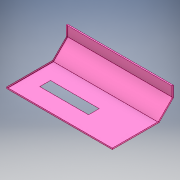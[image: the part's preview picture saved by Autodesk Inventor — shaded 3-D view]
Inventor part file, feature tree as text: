
AUTODESK INVENTOR PART (.ipt)
format: ipt  version: 2018 (Build 220112000, 112)  size: 258,560 bytes
history: native  units: mm
features: sheet_metal_op x13, sketch x6, other x5, extrude x1
ambient origin geometry x8: Origin, YZ Plane, XZ Plane, XY Plane, X Axis, Y Axis, Z Axis, Center Point
bodies: Solid1 (feature_tree)
feature tree (25):
  sheet_metal_op  "Face1"
  sheet_metal_op  "Flange1"
  sheet_metal_op  "Flange2"
  sheet_metal_op  "Flange3"
  extrude  "Extrusion1"  Depth=625.0mm
  sheet_metal_op  "Flange4"
  sketch  "Sketch1"  dims[d0=1410.0mm d1=625.0mm]
  other  "Plate1"
  sketch  "Sketch2"  dims[d2=1.6mm]
  other  "Plate2"
  sheet_metal_op  "Bend1"
  sheet_metal_op  "Corner1"
  sketch  "Sketch3"  dims[d3=1.6mm]
  other  "Plate3"
  sheet_metal_op  "Bend2"
  sheet_metal_op  "Corner2"
  sketch  "Sketch4"  dims[d4=0.8mm]
  other  "Plate4"
  sheet_metal_op  "Bend3"
  sheet_metal_op  "Corner3"
  sketch  "Sketch5"  dims[d5=3.2mm]
  sketch  "Sketch6"  dims[d6=1.6mm d7=270.0mm d8=45.0deg d9=1.6mm d10=6.4mm d11=1.6mm d12=1.6mm d13=1.6mm d14=0.8mm d15=3.2mm d16=1.6mm d17=150.0mm d18=45.0deg d19=1.6mm d20=6.4mm d21=1.6mm d22=1.6mm d23=1.6mm d24=0.8mm d25=3.2mm d26=1.6mm d27=20.0mm d28=90.0deg d29=1.6mm d30=6.4mm d31=1.6mm d32=1.6mm d33=650.0mm d34=140.0mm d36=195.0mm d37=10.0mm d38=0.0mm d39=1.6mm d40=0.8mm d41=3.2mm d42=1.6mm d43=75.0mm d44=13.962634mm d45=1.6mm d46=6.4mm d47=1.6mm d48=1.6mm d49=245.0mm]
  other  "Plate5"
  sheet_metal_op  "Bend4"
  sheet_metal_op  "Corner4"
